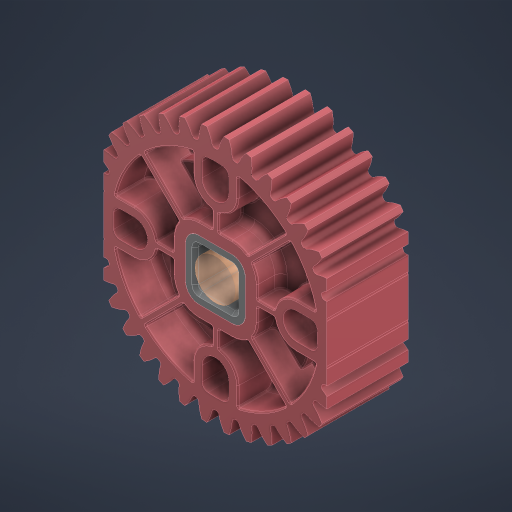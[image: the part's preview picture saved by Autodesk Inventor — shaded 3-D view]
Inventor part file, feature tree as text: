
AUTODESK INVENTOR PART (.ipt)
format: ipt  version: 2024 (Build 280153000, 153)  size: 2,316,800 bytes
history: native  units: in
note: dims shown in document units (in); Inventor stores cm internally (conversion verified against a paired STEP export)
features: other x3, extrude x2, sketch x1
ambient origin geometry x8: Origin, YZ Plane, XZ Plane, XY Plane, X Axis, Y Axis, Z Axis, Center Point
bodies: Solid1 (feature_tree), Solid2 (feature_tree)
feature tree (6):
  extrude  "Extrusion1"  Depth=0.3937in TaperAngle=0.0deg
  other  "Srf1"
  sketch  "Sketch4"  dims[d0=0.25in d1=0.3937in d2=0.0in d3=0.6875in d4=0.0in d5=0.0in]
  other  "276-7747-001_OVERMOLD Rev3_36T 24DP Gear Rev1_1:1"
  other  "276-7573-002 Rev7_2:1"
  extrude  "ExtrusionSrf1"  Depth=0.3937in
